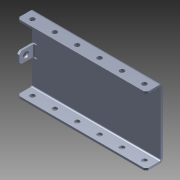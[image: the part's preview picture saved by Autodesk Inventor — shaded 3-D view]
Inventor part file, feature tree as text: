
AUTODESK INVENTOR PART (.ipt)
format: ipt  version: 2015 SP1 (Build 190203100, 203)  size: 151,552 bytes
history: native  units: in
note: dims shown in document units (in); Inventor stores cm internally (conversion verified against a paired STEP export)
features: chamfer x1, other x1, imported_body x1
ambient origin geometry x8: Origin, YZ Plane, XZ Plane, XY Plane, X Axis, Y Axis, Z Axis, Center Point
bodies: Body1 (feature_tree)
feature tree (3):
  chamfer  "Chamfer1"  [1 undecoded]
  other  "Battery Holder.ipt1"
  imported_body  "Base1"
note: 1 required parameter value undecoded (feature->parameter linkage not recoverable at this tier; creation-order binding heuristic only, values carry confidence <= 0.55)
